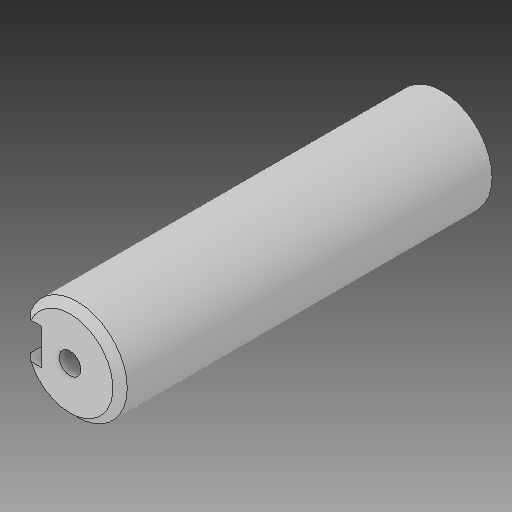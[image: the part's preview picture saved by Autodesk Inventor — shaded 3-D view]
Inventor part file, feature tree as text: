
AUTODESK INVENTOR PART (.ipt)
format: ipt  version: 2018 (Build 220112000, 112)  size: 117,248 bytes
history: native  units: mm
features: extrude x2, sketch x2, hole x1, plane x1, chamfer x1, projected_geometry x1
ambient origin geometry x8: Origin, YZ Plane, XZ Plane, XY Plane, X Axis, Y Axis, Z Axis, Center Point
bodies: Solid1 (feature_tree)
feature tree (8):
  extrude  "Extrusion1"  Depth=52.0mm TaperAngle=0.0deg
  hole  "Hole1"  [1 undecoded]
  plane  "Work Plane1"
  extrude  "Extrusion2"  TaperAngle=0.0deg  [1 undecoded]
  chamfer  "Chamfer1"  Distance=3.0mm
  sketch  "Sketch1"  dims[d0=14.0mm d1=52.0mm d2=0.0mm]
  sketch  "Sketch2"  dims[d3=10.0mm d4=10.0mm d5=3.0mm d6=6.0mm d7=4.0mm d8=2.0mm d9=90.0deg d10=13.0mm d11=0.0mm d12=5.0mm d14=0.0mm d17=3.0mm d18=0.0mm d19=1.0mm d20=2.0mm d21=45.0deg]
  projected_geometry  "Projected Loop1"
note: 2 required parameter values undecoded (feature->parameter linkage not recoverable at this tier; creation-order binding heuristic only, values carry confidence <= 0.55)
